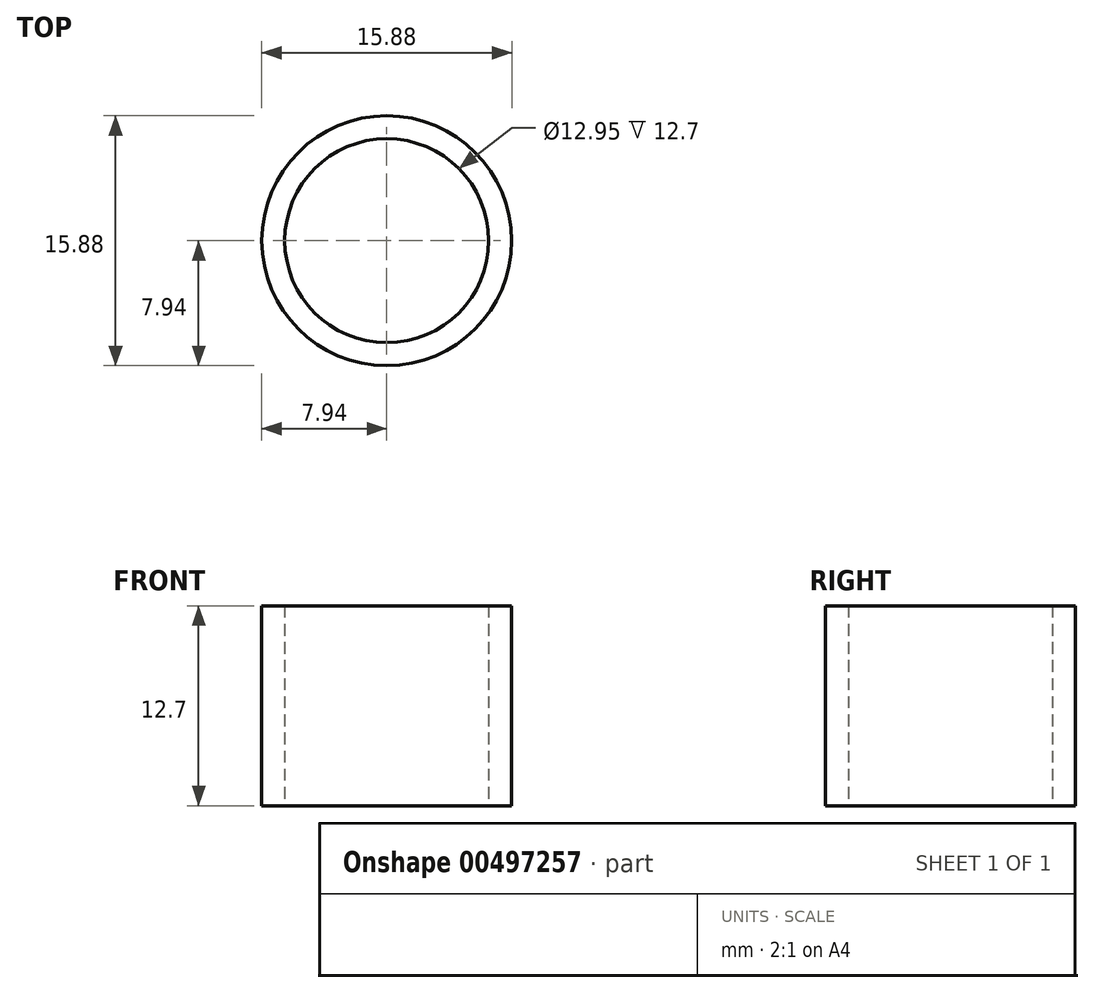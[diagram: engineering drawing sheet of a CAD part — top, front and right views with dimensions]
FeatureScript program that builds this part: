
annotation { "Feature Type Name" : "Feature", "Feature Type Description" : "" }
export const myFeature = defineFeature(function(context is Context, id is Id, definition is map)
    precondition{}
    {
        {
            var Q0;
            Q0=qCreatedBy(makeId("Top.planeOp"),FACE);
            var sketch = newSketch(context, id + "F0", { "sketchPlane" : qUnion([Q0])});
            skCircle(sketch, "E0", {"center": v(0, 0) * mm, "radius": 6.48 * mm});
            skCircle(sketch, "E1", {"center": v(0, 0) * mm, "radius": 7.94 * mm});
            skSolve(sketch);
        }
        {
            var Q0;
            Q0 = qSketchRegion(id + "F0", true);
            extrude(context, id + "F1", {"entities" : qUnion([Q0]), "depth" : 12.7 * mm, "offsetDistance" : 25.4 * mm});
        }
    });
